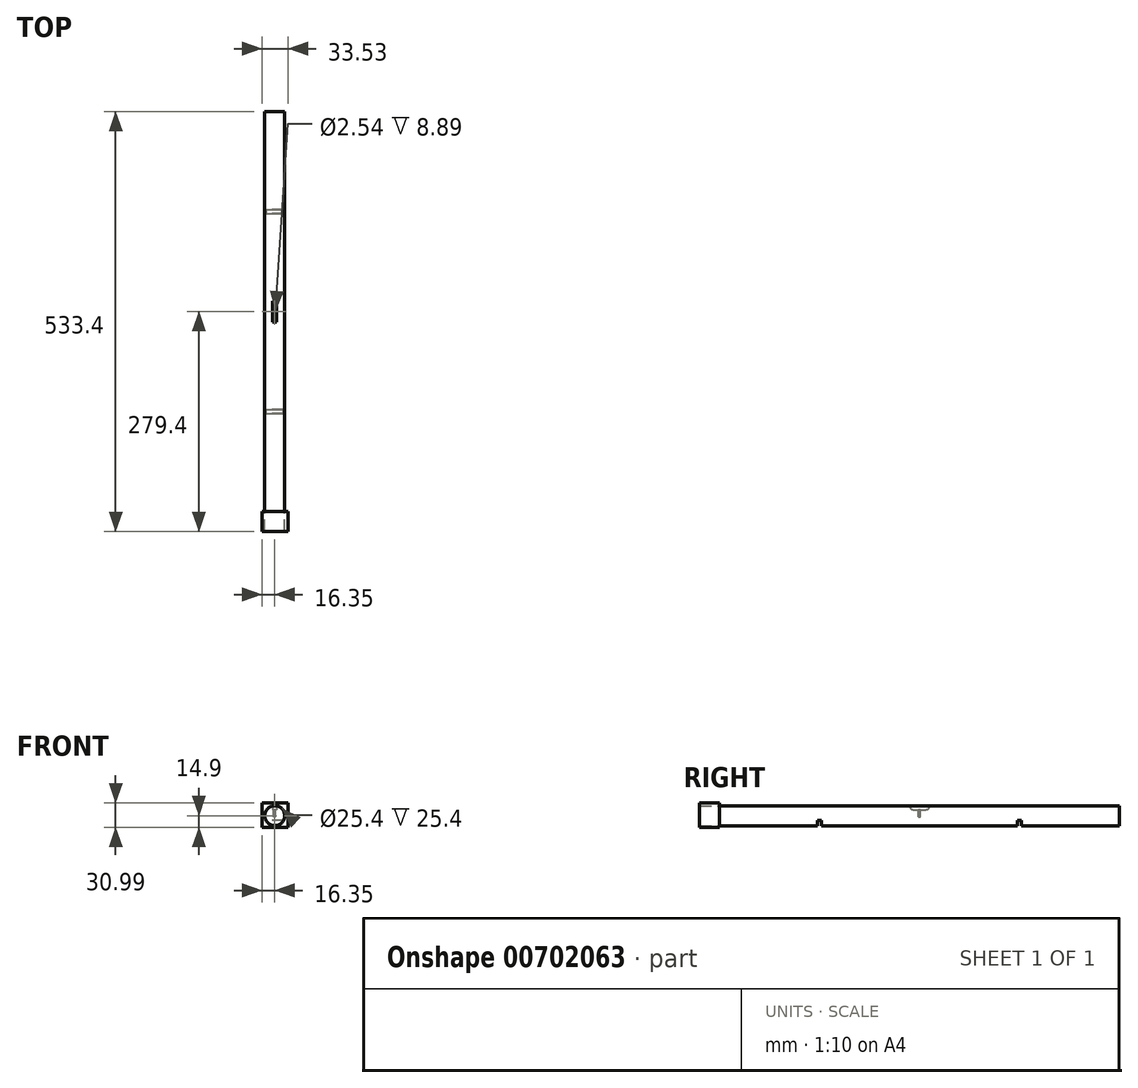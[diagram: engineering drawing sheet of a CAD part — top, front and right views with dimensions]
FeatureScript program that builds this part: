
annotation { "Feature Type Name" : "Feature", "Feature Type Description" : "" }
export const myFeature = defineFeature(function(context is Context, id is Id, definition is map)
    precondition{}
    {
        {
            var Q0;
            Q0=qCreatedBy(makeId("Front.planeOp"),FACE);
            var sketch = newSketch(context, id + "F0", { "sketchPlane" : qUnion([Q0])});
            skCircle(sketch, "E0", {"center": v(0, 0) * mm, "radius": 12.7 * mm});
            skSolve(sketch);
        }
        {
            var Q0;
            Q0=makeQuery(id+"F0.imprint","IMPRINT",FACE,{"disambiguationData":[TD([[makeQuery(id+"F0.imprint","IMPRINT",EDGE,{"derivedFrom":sQuery(id+"F0.wireOp",EDGE,"E0")}),1.0]])]});
            extrude(context, id + "F1", {"entities" : qUnion([Q0]), "depth" : 254 * mm, "offsetDistance" : 25.4 * mm});
        }
        {
            var Q0;
            Q0=qCreatedBy(makeId("Front.planeOp"),FACE);
            cPlane(context, id + "F2", {"entities" : qUnion([Q0]), "cplaneType" : CPlaneType.OFFSET, "offset" : 127 * mm, "width" : 152.4 * mm, "height" : 152.4 * mm});
        }
        {
            var Q0;
            Q0=qCreatedBy(id+"F2.planeOp",FACE);
            var sketch = newSketch(context, id + "F3", { "sketchPlane" : qUnion([Q0])});
            skLineSegment(sketch, "E1.bottom", {"start": v(19.35, -5.73) * mm, "end": v(-17.67, -5.73) * mm});
            skLineSegment(sketch, "E1.top", {"start": v(19.35, -13.9) * mm, "end": v(-17.67, -13.9) * mm});
            skLineSegment(sketch, "E1.left", {"start": v(19.35, -5.73) * mm, "end": v(19.35, -13.9) * mm});
            skLineSegment(sketch, "E1.right", {"start": v(-17.67, -5.73) * mm, "end": v(-17.67, -13.9) * mm});
            skSolve(sketch);
        }
        {
            var Q0;
            Q0=makeQuery(id+"F3.imprint","IMPRINT",FACE,{"disambiguationData":[TD([[makeQuery(id+"F3.imprint","IMPRINT",EDGE,{"derivedFrom":sQuery(id+"F3.wireOp",EDGE,"E1.bottom")}),1.0]])]});
            extrude(context, id + "F4", {"entities" : qUnion([Q0]), "operationType" : NewBodyOperationType.REMOVE, "depth" : 2.54 * mm, "offsetDistance" : 25.4 * mm, "hasSecondDirection" : true, "secondDirectionOppositeDirection" : true, "secondDirectionDepth" : 2.54 * mm});
        }
        {
            var Q0;
            Q0=makeQuery(id+"F1.opExtrude","SWEPT_BODY",BODY,{"disambiguationData":[OSD([sQuery(id+"F0.wireOp",EDGE,"E0")])]});
            var Q1;
            Q1=qCreatedBy(makeId("Front.planeOp"),FACE);
            mirror(context, id + "F5", {"operationType" : NewBodyOperationType.ADD, "entities" : qUnion([Q0]), "mirrorPlane" : qUnion([Q1])});
        }
        {
            var Q0;
            Q0=qCreatedBy(makeId("Right.planeOp"),FACE);
            var sketch = newSketch(context, id + "F6", { "sketchPlane" : qUnion([Q0])});
            skLineSegment(sketch, "E2.bottom", {"start": v(-13.34, 19.2) * mm, "end": v(13.7, 19.2) * mm});
            skLineSegment(sketch, "E2.top", {"start": v(-6.99, 7.47) * mm, "end": v(7.34, 7.47) * mm});
            skLineSegment(sketch, "E2.left", {"start": v(-13.34, 19.2) * mm, "end": v(-13.34, 13.82) * mm});
            skLineSegment(sketch, "E2.right", {"start": v(13.7, 19.2) * mm, "end": v(13.7, 13.82) * mm});
            skPoint(sketch, "E3.visualSharp", {"position": v(-13.34, 7.47) * mm});
            skArc(sketch, "E3.filletArc", {"start": v(-13.34, 13.82) * mm, "mid": v(-11.48, 9.33) * mm, "end": v(-6.99, 7.47) * mm});
            skPoint(sketch, "E4.visualSharp", {"position": v(13.7, 7.47) * mm});
            skArc(sketch, "E4.filletArc", {"start": v(7.34, 7.47) * mm, "mid": v(11.83, 9.33) * mm, "end": v(13.7, 13.82) * mm});
            skSolve(sketch);
        }
        {
            var Q0;
            Q0 = qSketchRegion(id + "F6", true);
            extrude(context, id + "F7", {"entities" : qUnion([Q0]), "operationType" : NewBodyOperationType.REMOVE, "depth" : 2.54 * mm, "offsetDistance" : 25.4 * mm, "hasSecondDirection" : true, "secondDirectionOppositeDirection" : true, "secondDirectionDepth" : 2.54 * mm});
        }
        {
            var Q0;
            Q0=makeQuery(id+"F7.boolean.opBoolean","COPY",FACE,{"derivedFrom":makeQuery(id+"F7.opExtrude","SWEPT_FACE",FACE,{"disambiguationData":[OSD([sQuery(id+"F6.wireOp",EDGE,"E2.top")])]})});
            var sketch = newSketch(context, id + "F8", { "sketchPlane" : qUnion([Q0])});
            skCircle(sketch, "E5", {"center": v(0, 0) * mm, "radius": 1.27 * mm});
            skSolve(sketch);
        }
        {
            var Q0;
            Q0 = qSketchRegion(id + "F8", true);
            extrude(context, id + "F9", {"entities" : qUnion([Q0]), "operationType" : NewBodyOperationType.REMOVE, "depth" : -8.9 * mm, "offsetDistance" : 25.4 * mm});
        }
        {
            var Q0;
            Q0=makeQuery(id+"F1.opExtrude","CAP_FACE",FACE,{"disambiguationData":[OSD([sQuery(id+"F0.wireOp",EDGE,"E0")])],"isStart":false});
            var sketch = newSketch(context, id + "F10", { "sketchPlane" : qUnion([Q0])});
            skSolve(sketch);
        }
        {
            var Q0;
            Q0=makeQuery(id+"F10.imprint","IMPRINT",FACE,{"disambiguationData":[TD([[makeQuery(id+"F10.imprint","IMPRINT",EDGE,{"derivedFrom":makeQuery(id+"F1.opExtrude","CAP_EDGE",EDGE,{"disambiguationData":[OSD([sQuery(id+"F0.wireOp",EDGE,"E0")])],"isStart":false})}),1.0]])]});
            var sketch = newSketch(context, id + "F11", { "sketchPlane" : qUnion([Q0])});
            skLineSegment(sketch, "E6.bottom", {"start": v(-16.35, 16.09) * mm, "end": v(17.18, 16.09) * mm});
            skLineSegment(sketch, "E6.top", {"start": v(-16.35, -14.9) * mm, "end": v(17.18, -14.9) * mm});
            skLineSegment(sketch, "E6.left", {"start": v(-16.35, 16.09) * mm, "end": v(-16.35, -14.9) * mm});
            skLineSegment(sketch, "E6.right", {"start": v(17.18, 16.09) * mm, "end": v(17.18, -14.9) * mm});
            skSolve(sketch);
        }
        {
            var Q0;
            Q0=makeQuery(id+"F11.imprint","IMPRINT",FACE,{"disambiguationData":[TD([[makeQuery(id+"F11.imprint","IMPRINT",EDGE,{"derivedFrom":sQuery(id+"F11.wireOp",EDGE,"E6.bottom")}),-1.0]])]});
            extrude(context, id + "F12", {"entities" : qUnion([Q0]), "depth" : 25.4 * mm, "offsetDistance" : 25.4 * mm});
        }
    });
